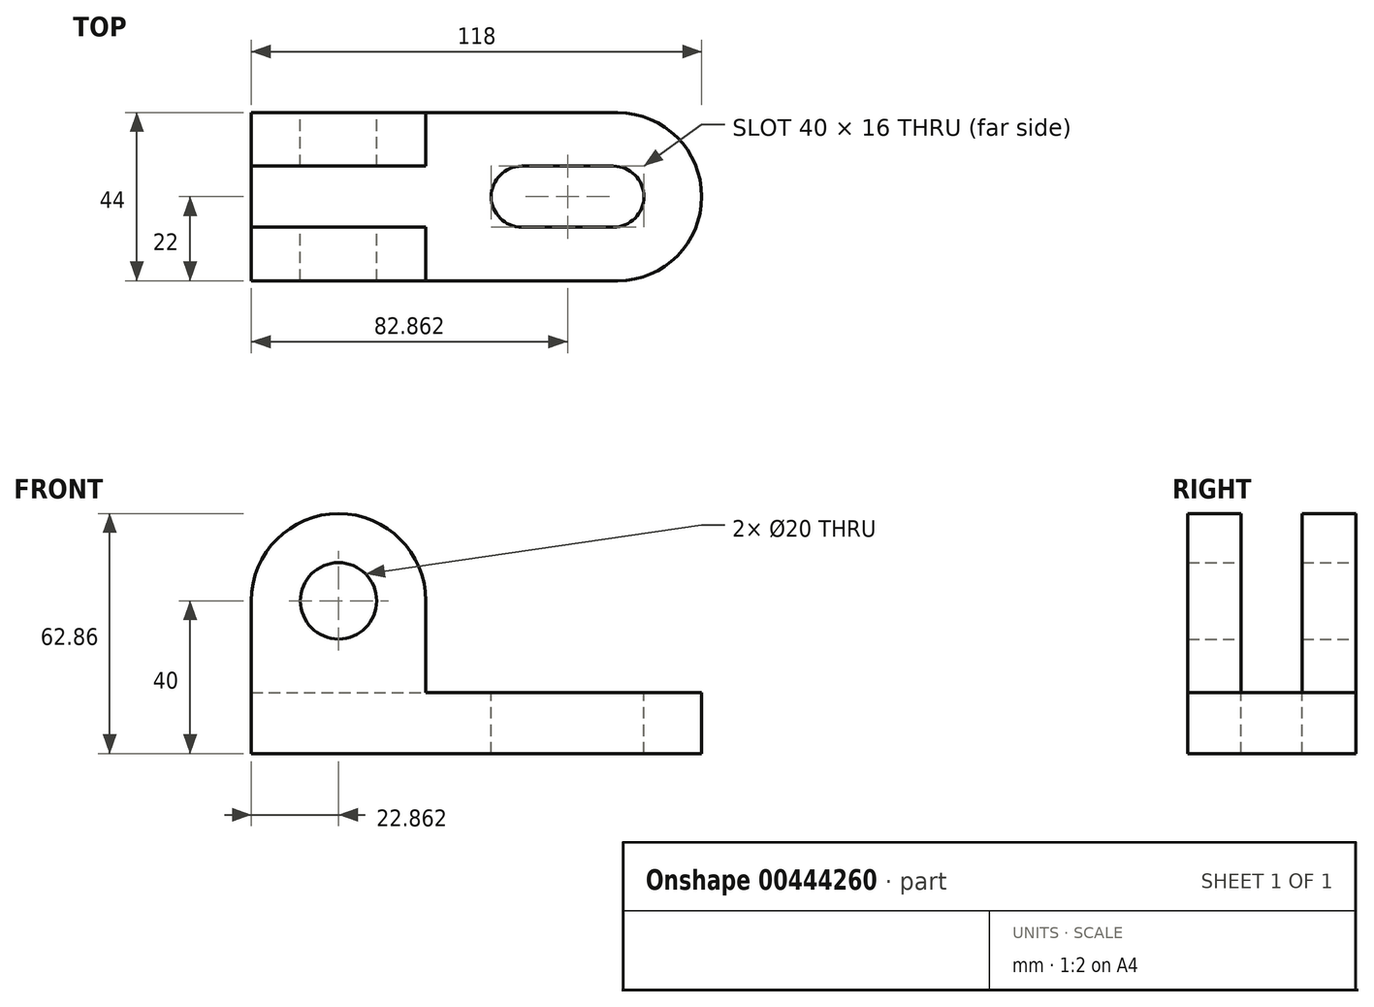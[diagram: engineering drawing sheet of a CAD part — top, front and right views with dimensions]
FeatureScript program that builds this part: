
annotation { "Feature Type Name" : "Feature", "Feature Type Description" : "" }
export const myFeature = defineFeature(function(context is Context, id is Id, definition is map)
    precondition{}
    {
        {
            var Q0;
            Q0=qCreatedBy(makeId("Front.planeOp"),FACE);
            var sketch = newSketch(context, id + "F0", { "sketchPlane" : qUnion([Q0])});
            skLineSegment(sketch, "E0.bottom", {"start": v(0, 0) * mm, "end": v(118, 0) * mm});
            skLineSegment(sketch, "E0.top", {"start": v(0, 16) * mm, "end": v(118, 16) * mm});
            skLineSegment(sketch, "E0.left", {"start": v(0, 0) * mm, "end": v(0, 16) * mm});
            skLineSegment(sketch, "E0.right", {"start": v(118, 0) * mm, "end": v(118, 16) * mm});
            skLineSegment(sketch, "E1.top", {"start": v(0, 71.9) * mm, "end": v(118, 71.9) * mm});
            skLineSegment(sketch, "E1.left", {"start": v(0, 16) * mm, "end": v(0, 71.9) * mm});
            skLineSegment(sketch, "E1.right", {"start": v(118, 16) * mm, "end": v(118, 71.9) * mm});
            skLineSegment(sketch, "E2", {"start": v(0, 0) * mm, "end": v(0, 40) * mm});
            skArc(sketch, "E3", {"start": v(45.72, 40) * mm, "mid": v(22.86, 62.86) * mm, "end": v(0, 40) * mm});
            skCircle(sketch, "E4", {"center": v(22.86, 40) * mm, "radius": 10 * mm});
            skLineSegment(sketch, "E5", {"start": v(45.72, 40) * mm, "end": v(45.72, 16) * mm});
            skSolve(sketch);
        }
        {
            var Q0;
            {var subQ0=sQuery(id+"F0.wireOp",EDGE,"E3");Q0=makeQuery(id+"F0.imprint","IMPRINT",FACE,{"disambiguationData":[TD([[makeQuery(id+"F0.imprint","IMPRINT",EDGE,{"derivedFrom":subQ0}),1.0]])]});}
            var Q1;
            {var subQ5=sQuery(id+"F0.wireOp",EDGE,"E0.bottom");Q1=makeQuery(id+"F0.imprint","IMPRINT",FACE,{"disambiguationData":[TD([[makeQuery(id+"F0.imprint","IMPRINT",EDGE,{"derivedFrom":subQ5}),1.0]])]});}
            extrude(context, id + "F1", {"entities" : qUnion([Q0, Q1]), "depth" : 22 * mm, "hasSecondDirection" : true, "secondDirectionOppositeDirection" : true, "secondDirectionDepth" : 22 * mm});
        }
        {
            var Q0;
            Q0=makeQuery(id+"F0.imprint","IMPRINT",FACE,{"disambiguationData":[TD([[makeQuery(id+"F0.imprint","IMPRINT",EDGE,{"derivedFrom":sQuery(id+"F0.wireOp",EDGE,"E1.top")}),-1.0]])]});
            var Q1;
            {var subQ0=sQuery(id+"F0.wireOp",EDGE,"E3");Q1=makeQuery(id+"F0.imprint","IMPRINT",FACE,{"disambiguationData":[TD([[makeQuery(id+"F0.imprint","IMPRINT",EDGE,{"derivedFrom":subQ0}),1.0]])]});}
            extrude(context, id + "F2", {"entities" : qUnion([Q0, Q1]), "operationType" : NewBodyOperationType.REMOVE, "oppositeDirection" : true, "depth" : 8 * mm, "hasSecondDirection" : true, "secondDirectionOppositeDirection" : false, "secondDirectionDepth" : 8 * mm});
        }
        {
            var Q0;
            Q0=makeQuery(id+"F1.opExtrude","CAP_EDGE",EDGE,{"disambiguationData":[OSD([sQuery(id+"F0.wireOp",EDGE,"E0.right")])],"isStart":false});
            var Q1;
            Q1=makeQuery(id+"F1.opExtrude","CAP_EDGE",EDGE,{"disambiguationData":[OSD([sQuery(id+"F0.wireOp",EDGE,"E0.right")])],"isStart":true});
            fillet(context, id + "F3", {"entities" : qUnion([Q0, Q1]), "radius" : 22 * mm, "tangentPropagation" : true, "allowEdgeOverflow" : false});
        }
        {
            var Q0;
            {var subQ0=sQuery(id+"F0.wireOp",EDGE,"E0.top");Q0=makeQuery(id+"F2.boolean.opBoolean","MERGE",FACE,{"derivedFrom":[makeQuery(id+"F1.opExtrude","SWEPT_FACE",FACE,{"disambiguationData":[OSD([subQ0])]}),makeQuery(id+"F2.opExtrude","SWEPT_FACE",FACE,{"disambiguationData":[OSD([subQ0])]})]});}
            var sketch = newSketch(context, id + "F4", { "sketchPlane" : qUnion([Q0])});
            skLineSegment(sketch, "E6.0", {"start": v(32.86, -22) * mm, "end": v(12.86, -22) * mm});
            skPoint(sketch, "E7", {"position": v(22.86, -22) * mm});
            skLineSegment(sketch, "E8", {"start": v(70.86, 0) * mm, "end": v(94.86, 0) * mm});
            skArc(sketch, "E9.0.startCap", {"start": v(70.86, -8) * mm, "mid": v(62.86, 0) * mm, "end": v(70.86, 8) * mm});
            skArc(sketch, "E9.0.endCap", {"start": v(94.86, 8) * mm, "mid": v(102.86, 0) * mm, "end": v(94.86, -8) * mm});
            skLineSegment(sketch, "E9.0.left", {"start": v(70.86, 8) * mm, "end": v(94.86, 8) * mm});
            skLineSegment(sketch, "E9.0.right", {"start": v(70.86, -8) * mm, "end": v(94.86, -8) * mm});
            skSolve(sketch);
        }
        {
            var Q0;
            Q0 = qSketchRegion(id + "F4", true);
            extrude(context, id + "F5", {"entities" : qUnion([Q0]), "operationType" : NewBodyOperationType.REMOVE, "oppositeDirection" : true, "depth" : 25 * mm});
        }
    });
